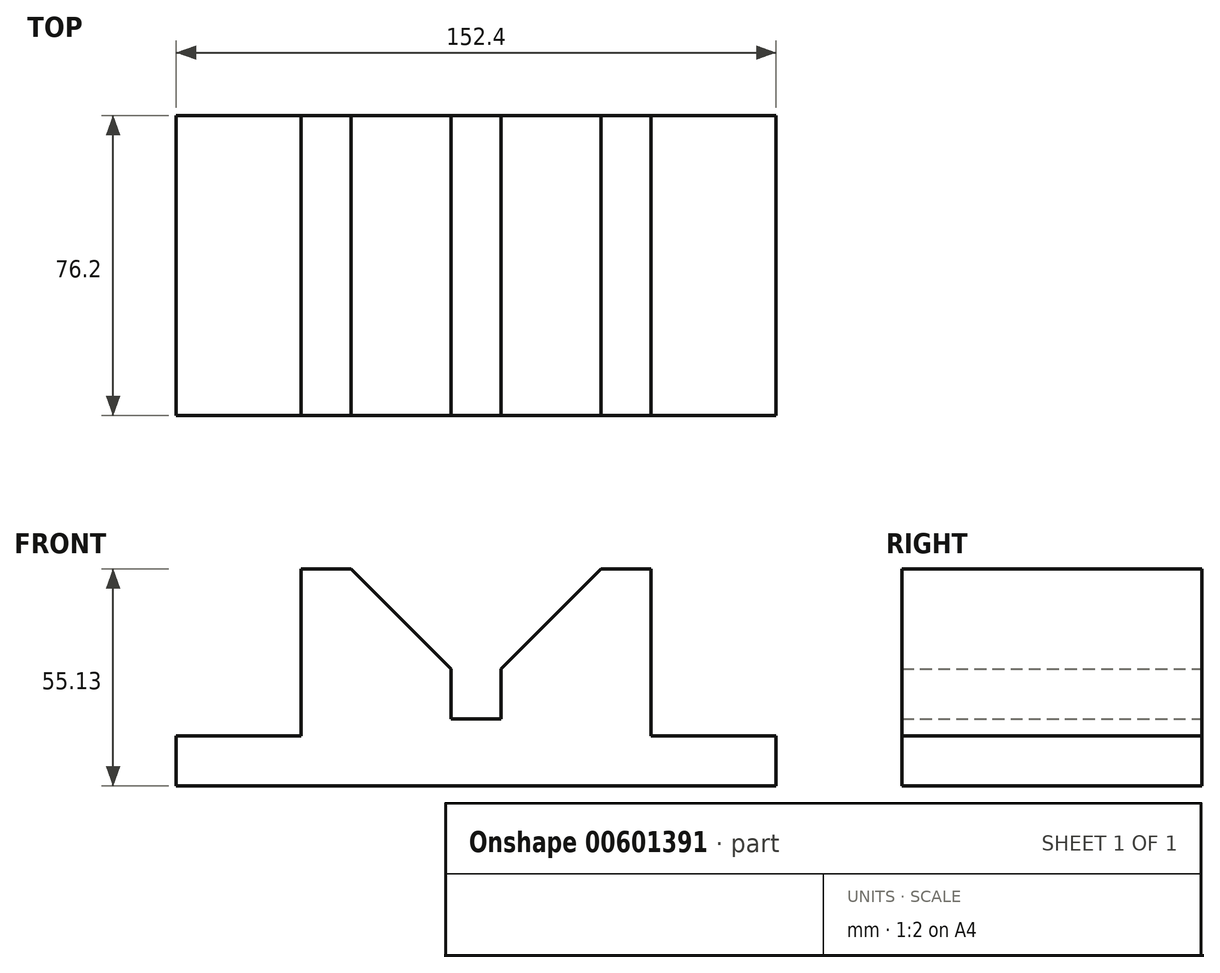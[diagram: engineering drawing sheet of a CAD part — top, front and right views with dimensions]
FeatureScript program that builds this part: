
annotation { "Feature Type Name" : "Feature", "Feature Type Description" : "" }
export const myFeature = defineFeature(function(context is Context, id is Id, definition is map)
    precondition{}
    {
        {
            var Q0;
            Q0=qCreatedBy(makeId("Front.planeOp"),FACE);
            var sketch = newSketch(context, id + "F0", { "sketchPlane" : qUnion([Q0])});
            skLineSegment(sketch, "E0", {"start": v(-88.5, -11.69) * mm, "end": v(-56.74, -11.69) * mm});
            skLineSegment(sketch, "E1", {"start": v(-56.74, -11.69) * mm, "end": v(-56.74, 30.74) * mm});
            skLineSegment(sketch, "E2", {"start": v(-56.74, 30.74) * mm, "end": v(-44.04, 30.74) * mm});
            skLineSegment(sketch, "E3", {"start": v(-44.04, 30.74) * mm, "end": v(-18.64, 5.34) * mm});
            skLineSegment(sketch, "E4", {"start": v(-18.64, 5.34) * mm, "end": v(-18.64, -7.36) * mm});
            skLineSegment(sketch, "E5", {"start": v(-18.64, -7.36) * mm, "end": v(-5.94, -7.36) * mm});
            skLineSegment(sketch, "E6", {"start": v(-5.94, -7.36) * mm, "end": v(-5.94, 5.34) * mm});
            skLineSegment(sketch, "E7", {"start": v(-5.94, 5.34) * mm, "end": v(19.46, 30.74) * mm});
            skLineSegment(sketch, "E8", {"start": v(19.46, 30.74) * mm, "end": v(32.16, 30.74) * mm});
            skLineSegment(sketch, "E9", {"start": v(32.16, 30.74) * mm, "end": v(32.16, -11.69) * mm});
            skLineSegment(sketch, "E10", {"start": v(32.16, -11.69) * mm, "end": v(63.9, -11.69) * mm});
            skLineSegment(sketch, "E11", {"start": v(63.9, -11.69) * mm, "end": v(63.9, -24.39) * mm});
            skLineSegment(sketch, "E12", {"start": v(63.9, -24.39) * mm, "end": v(-88.5, -24.39) * mm});
            skLineSegment(sketch, "E13", {"start": v(-88.5, -24.39) * mm, "end": v(-88.5, -11.69) * mm});
            skSolve(sketch);
        }
        {
            var Q0;
            Q0=makeQuery(id+"F0.imprint","IMPRINT",FACE,{"disambiguationData":[TD([[makeQuery(id+"F0.imprint","IMPRINT",EDGE,{"derivedFrom":sQuery(id+"F0.wireOp",EDGE,"E0")}),-1.0]])]});
            extrude(context, id + "F1", {"entities" : qUnion([Q0]), "depth" : 76.2 * mm, "offsetDistance" : 25.4 * mm});
        }
    });
